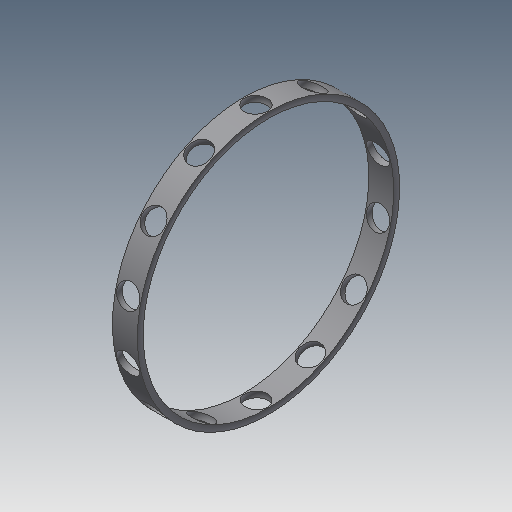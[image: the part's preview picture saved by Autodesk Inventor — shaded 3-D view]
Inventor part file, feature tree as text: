
AUTODESK INVENTOR PART (.ipt)
format: ipt  version: 2019.4 (Build 234330000, 330)  size: 264,192 bytes
history: native  units: mm
features: other x105, revolve x2, sketch x2, pattern_circular x1
ambient origin geometry x8: Origin, YZ Plane, XZ Plane, XY Plane, X Axis, Y Axis, Z Axis, Center Point
bodies: Solid1 (feature_tree)
feature tree (110):
  revolve  "Revolution1"  Angle=360.0deg
  revolve  "Revolution2"  [1 undecoded]
  pattern_circular  "Circular Pattern1"  [2 undecoded]
  other  "1_XY"
  other  "1_YZ"
  other  "1_ZX"
  other  "1_X"
  other  "1_Y"
  other  "1_Z"
  other  "1_Center"
  other  "2_1_XY"
  other  "2_1_YZ"
  other  "2_1_ZX"
  other  "2_1_X"
  other  "2_1_Y"
  other  "2_1_Z"
  other  "2_1_Center"
  other  "2_10_XY"
  other  "2_10_YZ"
  other  "2_10_ZX"
  other  "2_10_X"
  other  "2_10_Y"
  other  "2_10_Z"
  other  "2_10_Center"
  other  "2_11_XY"
  other  "2_11_YZ"
  other  "2_11_ZX"
  other  "2_11_X"
  other  "2_11_Y"
  other  "2_11_Z"
  other  "2_11_Center"
  other  "2_12_XY"
  other  "2_12_YZ"
  other  "2_12_ZX"
  other  "2_12_X"
  other  "2_12_Y"
  other  "2_12_Z"
  other  "2_12_Center"
  other  "2_13_XY"
  other  "2_13_YZ"
  other  "2_13_ZX"
  other  "2_13_X"
  other  "2_13_Y"
  other  "2_13_Z"
  other  "2_13_Center"
  other  "2_14_XY"
  other  "2_14_YZ"
  other  "2_14_ZX"
  other  "2_14_X"
  other  "2_14_Y"
  other  "2_14_Z"
  other  "2_14_Center"
  other  "2_2_XY"
  other  "2_2_YZ"
  other  "2_2_ZX"
  other  "2_2_X"
  other  "2_2_Y"
  other  "2_2_Z"
  other  "2_2_Center"
  other  "2_3_XY"
  other  "2_3_YZ"
  other  "2_3_ZX"
  other  "2_3_X"
  other  "2_3_Y"
  other  "2_3_Z"
  other  "2_3_Center"
  other  "2_4_XY"
  other  "2_4_YZ"
  other  "2_4_ZX"
  other  "2_4_X"
  other  "2_4_Y"
  other  "2_4_Z"
  other  "2_4_Center"
  other  "2_5_XY"
  other  "2_5_YZ"
  other  "2_5_ZX"
  other  "2_5_X"
  other  "2_5_Y"
  other  "2_5_Z"
  other  "2_5_Center"
  other  "2_6_XY"
  other  "2_6_YZ"
  other  "2_6_ZX"
  other  "2_6_X"
  other  "2_6_Y"
  other  "2_6_Z"
  other  "2_6_Center"
  other  "2_7_XY"
  other  "2_7_YZ"
  other  "2_7_ZX"
  other  "2_7_X"
  other  "2_7_Y"
  other  "2_7_Z"
  other  "2_7_Center"
  other  "2_8_XY"
  other  "2_8_YZ"
  other  "2_8_ZX"
  other  "2_8_X"
  other  "2_8_Y"
  other  "2_8_Z"
  other  "2_8_Center"
  other  "2_9_XY"
  other  "2_9_YZ"
  other  "2_9_ZX"
  other  "2_9_X"
  other  "2_9_Y"
  other  "2_9_Z"
  other  "2_9_Center"
  sketch  "Sketch_6"  dims[d2=140.0mm d3=4.48799mm]
  sketch  "Sketch_2"  dims[d0=360.0deg d1=360.0deg]
note: 3 required parameter values undecoded (feature->parameter linkage not recoverable at this tier; creation-order binding heuristic only, values carry confidence <= 0.55)
